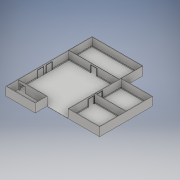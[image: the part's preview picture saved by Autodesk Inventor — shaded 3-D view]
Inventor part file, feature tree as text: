
AUTODESK INVENTOR PART (.ipt)
format: ipt  version: 2017 (Build 210142000, 142)  size: 668,672 bytes
history: native  units: in
note: dims shown in document units (in); Inventor stores cm internally (conversion verified against a paired STEP export)
features: sketch x48, extrude x46, fillet x2, helix x1, other x1
ambient origin geometry x8: Origin, YZ Plane, XZ Plane, XY Plane, X Axis, Y Axis, Z Axis, Center Point
bodies: Solid1 (feature_tree)
feature tree (98):
  extrude  "Door Frame CR"  Depth=7.5in
  extrude  "Door Frame left Extruded"  Depth=11.0in
  extrude  "Door Frame right Extruded"  Depth=0.35in TaperAngle=0.0deg
  extrude  "Floor"  Depth=27.0in TaperAngle=0.0deg
  extrude  "Walls"  Depth=30.0in TaperAngle=0.0deg
  extrude  "Door Fram ex"  Depth=10.8125in TaperAngle=0.0deg
  fillet  "Dorr Fillet"  Radius=0.3in
  fillet  "Door Fillet"  Radius=0.3in
  extrude  "Door floor"  Depth=0.3125in TaperAngle=0.0deg
  extrude  "wall board middle"  Depth=0.02in
  extrude  "Wall board left"  Depth=0.35in
  extrude  "Wall board right"  Depth=1.455in
  extrude  "Wall board door"  Depth=1.4574in
  extrude  "Door mid"  Depth=0.1in TaperAngle=0.0deg
  extrude  "Main wall left"  Depth=0.1in TaperAngle=0.0deg
  extrude  "Main wall right"  Depth=65.5in
  extrude  "prob the floor"  Depth=65.5in
  extrude  "wall board front main 1"  TaperAngle=0.0deg  [1 undecoded]
  extrude  "wall board front main 2"  TaperAngle=0.0deg  [1 undecoded]
  extrude  "wall board front left"  Depth=0.1in TaperAngle=0.0deg
  extrude  "wall board front right"  Depth=0.1in TaperAngle=0.0deg
  extrude  "Right doors"  Depth=7.5in
  sketch  "Sketch33"  dims[d67=0.1in d68=0.0in d69=7.5in]
  extrude  "Right doors head"  Depth=11.0in
  sketch  "Sketch35"  dims[d72=11.0in d73=3.0in d74=0.05in d75=0.0in d76=0.0in]
  extrude  "Right doors frame mid"  Depth=0.05in TaperAngle=0.0deg
  extrude  "right doors frame into"  Depth=1.72in
  extrude  "Room 2 & 3 wall "  Depth=0.3049in
  extrude  "Room 3 wall right"  Depth=0.3in TaperAngle=0.0deg
  extrude  "Room 3 wall mid"  Depth=40.0in TaperAngle=0.0deg
  extrude  "Room 3 Floor"  Depth=0.6in
  extrude  "Room 2 mid wall"  Depth=40.0in TaperAngle=0.0deg
  extrude  "Room 2 wall left"  Depth=10.8in
  extrude  "Room 2 floor"  Depth=40.0in TaperAngle=0.0deg
  extrude  "Room 2 wall board left"  Depth=10.8in
  extrude  "Room 3 wall board left"  Depth=0.6in
  extrude  "Room 2 & 3 wall board mid"  Depth=39.9in TaperAngle=0.0deg
  extrude  "Room 3 wall board right"  Depth=1.255in
  extrude  "Room 2 wall board right"  Depth=1.255in
  extrude  "Room 3 wall board door"  Depth=1.255in
  extrude  "Room 2 wall board door"  Depth=1.255in
  extrude  "Fake Door Frame"  Depth=1.255in
  extrude  "My mistake ;-;"  Depth=1.255in
  extrude  "Closet main wall"  Depth=0.1in TaperAngle=0.0deg
  extrude  "Closet left and right wall"  Depth=0.15in TaperAngle=0.0deg
  extrude  "Closet back wall"  Depth=37.0in TaperAngle=0.0deg
  extrude  "Closet Floor"  Depth=0.6in
  extrude  "Closet Outter wall board"  Depth=0.6in
  extrude  "Closet Door Frame"  Depth=15.0in TaperAngle=0.0deg
  extrude  "Extrusion47"  Depth=0.315in TaperAngle=0.0deg
  helix  "Coil1"  [1 undecoded]
  sketch  "Sketch1"  dims[d0=9.0in d1=7.5in]
  sketch  "Sketch2"  dims[d2=2.0in d3=11.0in]
  sketch  "Sketch4"  dims[d4=11.5in d5=0.35in d6=0.0in]
  sketch  "Sketch5"  dims[d7=27.0in d8=0.0in d9=27.0in d10=0.0in]
  sketch  "Sketch7"  dims[d11=0.2in d12=30.0in d13=0.0in]
  other  "Door Frame"
  sketch  "Sketch9"  dims[d21=0.5in d22=10.8125in d23=0.0in d27=0.3in d28=0.3in]
  sketch  "Sketch13"  dims[d29=0.3in d30=0.3125in d31=0.0in]
  sketch  "Sketch14"  dims[d32=0.02in d33=0.02in]
  sketch  "Sketch16"  dims[d34=0.35in d35=0.0in d36=1.3in]
  sketch  "Sketch20"  dims[d37=0.1in d38=0.0in d39=1.455in]
  sketch  "Sketch22"  dims[d40=0.1in d41=0.0in d42=1.4574in]
  sketch  "Sketch23"  dims[d43=1.457in d44=0.1in d45=0.0in]
  sketch  "Sketch24"  dims[d47=1.457in d49=0.1in d50=0.0in]
  sketch  "Sketch26"  dims[d51=0.35in d52=0.0in d53=65.5in]
  sketch  "Sketch27"  dims[d54=0.0in d55=65.5in]
  sketch  "Sketch28"  dims[d56=65.5in d57=0.0in]
  sketch  "Sketch30"  dims[d58=65.5in d59=0.0in]
  sketch  "Sketch31"  dims[d60=1.4574in d61=0.1in d62=0.0in]
  sketch  "Sketch32"  dims[d63=0.1in d64=0.0in d65=0.1in d66=0.0in]
  sketch  "Sketch34"  dims[d70=7.5in d71=11.0in]
  sketch  "Sketch36"  dims[d77=1.72in d78=1.72in]
  sketch  "Sketch38"  dims[d79=20.375in d80=0.0in d81=0.3049in]
  sketch  "Sketch41"  dims[d82=0.3049in d87=0.3in d88=0.0in]
  sketch  "Sketch44"  dims[d90=0.3in d91=0.0in d94=40.0in d95=0.0in]
  sketch  "Sketch45"  dims[d96=10.8in d97=0.6in]
  sketch  "Sketch47"  dims[d98=10.8in d99=40.0in d100=0.0in]
  sketch  "Sketch48"  dims[d101=0.6in d102=10.8in]
  sketch  "Sketch49"  dims[d103=33.5in d104=0.0in d105=40.0in d106=0.0in]
  sketch  "Sketch50"  dims[d107=0.6in d108=10.8in]
  sketch  "Sketch54"  dims[d109=33.5in d110=0.0in d111=0.6in]
  sketch  "Sketch55"  dims[d112=10.8in d113=39.9in d114=0.0in]
  sketch  "Sketch56"  dims[d115=40.0in d116=0.0in d117=1.255in]
  sketch  "Sketch57"  dims[d118=0.1in d119=0.0in d120=1.255in]
  sketch  "Sketch58"  dims[d121=0.1in d122=0.0in d123=1.255in]
  sketch  "Sketch59"  dims[d124=0.1in d125=0.0in d126=1.255in]
  sketch  "Sketch60"  dims[d127=0.1in d128=0.0in d129=1.255in]
  sketch  "Sketch62"  dims[d130=0.1in d131=0.0in d132=1.255in]
  sketch  "Sketch64"  dims[d133=0.1in d134=0.0in d135=0.1in d136=0.0in]
  sketch  "Sketch67"  dims[d137=0.315in d138=0.0in d139=0.15in d140=0.0in]
  sketch  "Sketch68"  dims[d141=0.6in d142=37.0in d143=0.0in]
  sketch  "Sketch69"  dims[d144=0.6in d145=0.6in]
  sketch  "Sketch70"  dims[d146=15.0in d147=0.0in d148=0.6in]
  sketch  "Sketch73"  dims[d149=36.4375in d150=0.0in d151=15.0in d152=0.0in]
  sketch  "Sketch74"  dims[d153=0.15in d154=0.0in d160=0.315in d161=0.0in d162=3.0in d163=0.0in]
  sketch  "Sketch76"  dims[d164=96.0in d165=1.0in d166=0.5906in d167=0.0in d168=90.0deg d169=90.0deg d170=0.0in d171=0.0in]
  sketch  "Sketch77"
note: 3 required parameter values undecoded (feature->parameter linkage not recoverable at this tier; creation-order binding heuristic only, values carry confidence <= 0.55)
